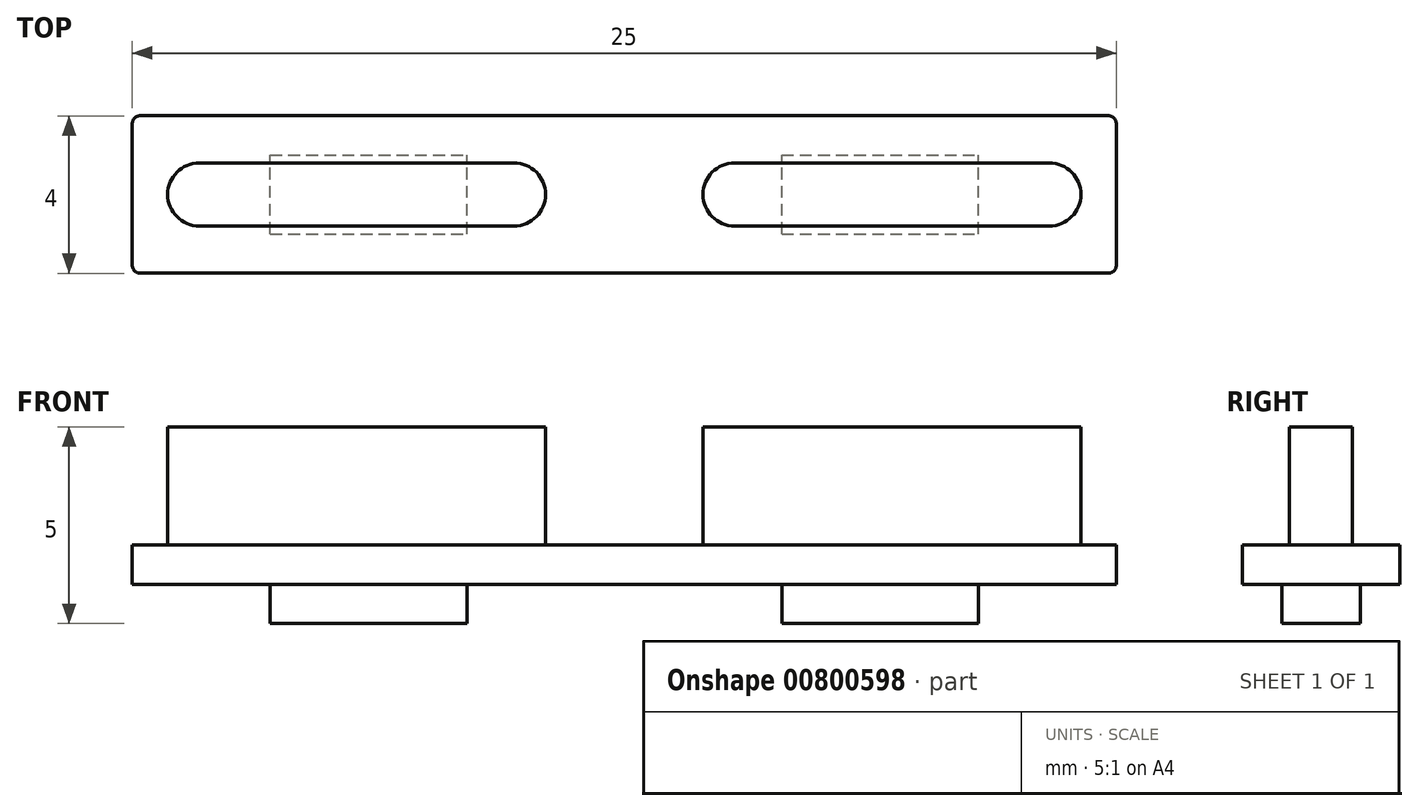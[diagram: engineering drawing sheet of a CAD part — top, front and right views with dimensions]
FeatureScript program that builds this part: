
annotation { "Feature Type Name" : "Feature", "Feature Type Description" : "" }
export const myFeature = defineFeature(function(context is Context, id is Id, definition is map)
    precondition{}
    {
        {
            var Q0;
            Q0=qCreatedBy(makeId("Top.planeOp"),FACE);
            var sketch = newSketch(context, id + "F0", { "sketchPlane" : qUnion([Q0])});
            skLineSegment(sketch, "E0.bottom", {"start": v(-2.37, 0.77) * mm, "end": v(22.63, 0.77) * mm});
            skLineSegment(sketch, "E0.top", {"start": v(-2.37, -3.23) * mm, "end": v(22.63, -3.23) * mm});
            skLineSegment(sketch, "E0.left", {"start": v(-2.37, 0.77) * mm, "end": v(-2.37, -3.23) * mm});
            skLineSegment(sketch, "E0.right", {"start": v(22.63, 0.77) * mm, "end": v(22.63, -3.23) * mm});
            skLineSegment(sketch, "E1", {"start": v(10.13, 0.77) * mm, "end": v(10.13, -3.23) * mm, "construction": true});
            skSolve(sketch);
        }
        {
            var Q0;
            Q0 = qSketchRegion(id + "F0", true);
            extrude(context, id + "F1", {"entities" : qUnion([Q0]), "depth" : 1 * mm, "offsetDistance" : 25 * mm});
        }
        {
            var Q0;
            Q0=makeQuery(id+"F1.opExtrude","CAP_FACE",FACE,{"disambiguationData":[OSD([sQuery(id+"F0.wireOp",EDGE,"E0.bottom"),sQuery(id+"F0.wireOp",EDGE,"E0.top"),sQuery(id+"F0.wireOp",EDGE,"E0.left"),sQuery(id+"F0.wireOp",EDGE,"E0.right")])],"isStart":false});
            var sketch = newSketch(context, id + "F2", { "sketchPlane" : qUnion([Q0])});
            skLineSegment(sketch, "E2.top", {"start": v(-0.67, -2.03) * mm, "end": v(7.33, -2.03) * mm});
            skArc(sketch, "E3", {"start": v(7.33, -2.03) * mm, "mid": v(8.13, -1.23) * mm, "end": v(7.33, -0.43) * mm});
            skPoint(sketch, "E4", {"position": v(22.63, -1.23) * mm});
            skPoint(sketch, "E5", {"position": v(-2.37, -1.23) * mm});
            skLineSegment(sketch, "E6", {"start": v(22.63, -1.23) * mm, "end": v(-2.37, -1.23) * mm, "construction": true});
            skLineSegment(sketch, "E7", {"start": v(7.33, -0.43) * mm, "end": v(-0.67, -0.43) * mm});
            skArc(sketch, "E8", {"start": v(-0.67, -0.43) * mm, "mid": v(-1.47, -1.23) * mm, "end": v(-0.67, -2.03) * mm});
            skPoint(sketch, "E9", {"position": v(10.13, -3.23) * mm});
            skPoint(sketch, "E10", {"position": v(10.13, 0.77) * mm});
            skLineSegment(sketch, "E11", {"start": v(10.13, -3.23) * mm, "end": v(10.13, 0.77) * mm, "construction": true});
            skLineSegment(sketch, "E12.top", {"start": v(12.93, -2.03) * mm, "end": v(20.93, -2.03) * mm});
            skArc(sketch, "E13", {"start": v(20.93, -2.03) * mm, "mid": v(21.73, -1.23) * mm, "end": v(20.93, -0.43) * mm});
            skLineSegment(sketch, "E14", {"start": v(20.93, -0.43) * mm, "end": v(12.93, -0.43) * mm});
            skArc(sketch, "E15", {"start": v(12.93, -0.43) * mm, "mid": v(12.13, -1.23) * mm, "end": v(12.93, -2.03) * mm});
            skSolve(sketch);
        }
        {
            var Q0;
            Q0=makeQuery(id+"F2.imprint","IMPRINT",FACE,{"disambiguationData":[TD([[makeQuery(id+"F2.imprint","IMPRINT",EDGE,{"derivedFrom":sQuery(id+"F2.wireOp",EDGE,"E2.top")}),1.0]])]});
            var Q1;
            Q1=makeQuery(id+"F2.imprint","IMPRINT",FACE,{"disambiguationData":[TD([[makeQuery(id+"F2.imprint","IMPRINT",EDGE,{"derivedFrom":sQuery(id+"F2.wireOp",EDGE,"E12.top")}),1.0]])]});
            extrude(context, id + "F3", {"entities" : qUnion([Q0, Q1]), "operationType" : NewBodyOperationType.ADD, "depth" : 3 * mm, "offsetDistance" : 25 * mm});
        }
        {
            var Q0;
            Q0=makeQuery(id+"F1.opExtrude","SWEPT_EDGE",EDGE,{"disambiguationData":[OSD([sQuery(id+"F0.wireOp",EDGE,"E0.bottom"),sQuery(id+"F0.wireOp",EDGE,"E0.right")])]});
            var Q1;
            Q1=makeQuery(id+"F1.opExtrude","SWEPT_EDGE",EDGE,{"disambiguationData":[OSD([sQuery(id+"F0.wireOp",EDGE,"E0.top"),sQuery(id+"F0.wireOp",EDGE,"E0.right")])]});
            var Q2;
            Q2=makeQuery(id+"F1.opExtrude","SWEPT_EDGE",EDGE,{"disambiguationData":[OSD([sQuery(id+"F0.wireOp",EDGE,"E0.top"),sQuery(id+"F0.wireOp",EDGE,"E0.left")])]});
            var Q3;
            Q3=makeQuery(id+"F1.opExtrude","SWEPT_EDGE",EDGE,{"disambiguationData":[OSD([sQuery(id+"F0.wireOp",EDGE,"E0.bottom"),sQuery(id+"F0.wireOp",EDGE,"E0.left")])]});
            fillet(context, id + "F4", {"entities" : qUnion([Q0, Q1, Q2, Q3]), "radius" : 0.2 * mm, "tangentPropagation" : true, "allowEdgeOverflow" : false});
        }
        {
            var Q0;
            Q0=makeQuery(id+"F1.opExtrude","CAP_FACE",FACE,{"disambiguationData":[OSD([sQuery(id+"F0.wireOp",EDGE,"E0.bottom"),sQuery(id+"F0.wireOp",EDGE,"E0.top"),sQuery(id+"F0.wireOp",EDGE,"E0.left"),sQuery(id+"F0.wireOp",EDGE,"E0.right")])],"isStart":true});
            var sketch = newSketch(context, id + "F5", { "sketchPlane" : qUnion([Q0])});
            skLineSegment(sketch, "E16.bottom", {"start": v(1.13, 2.23) * mm, "end": v(6.13, 2.23) * mm});
            skLineSegment(sketch, "E16.top", {"start": v(1.13, 0.23) * mm, "end": v(6.13, 0.23) * mm});
            skLineSegment(sketch, "E16.left", {"start": v(1.13, 2.23) * mm, "end": v(1.13, 0.23) * mm});
            skLineSegment(sketch, "E16.right", {"start": v(6.13, 2.23) * mm, "end": v(6.13, 0.23) * mm});
            skLineSegment(sketch, "E17.bottom", {"start": v(14.13, 2.23) * mm, "end": v(19.13, 2.23) * mm});
            skLineSegment(sketch, "E17.top", {"start": v(14.13, 0.23) * mm, "end": v(19.13, 0.23) * mm});
            skLineSegment(sketch, "E17.left", {"start": v(14.13, 2.23) * mm, "end": v(14.13, 0.23) * mm});
            skLineSegment(sketch, "E17.right", {"start": v(19.13, 2.23) * mm, "end": v(19.13, 0.23) * mm});
            skPoint(sketch, "E18", {"position": v(-2.37, 1.23) * mm});
            skPoint(sketch, "E19", {"position": v(22.63, 1.23) * mm});
            skLineSegment(sketch, "E20", {"start": v(-2.37, 1.23) * mm, "end": v(22.63, 1.23) * mm, "construction": true});
            skSolve(sketch);
        }
        {
            var Q0;
            Q0=makeQuery(id+"F5.imprint","IMPRINT",FACE,{"disambiguationData":[TD([[makeQuery(id+"F5.imprint","IMPRINT",EDGE,{"derivedFrom":sQuery(id+"F5.wireOp",EDGE,"E16.bottom")}),-1.0]])]});
            var Q1;
            Q1=makeQuery(id+"F5.imprint","IMPRINT",FACE,{"disambiguationData":[TD([[makeQuery(id+"F5.imprint","IMPRINT",EDGE,{"derivedFrom":sQuery(id+"F5.wireOp",EDGE,"E17.bottom")}),-1.0]])]});
            extrude(context, id + "F6", {"entities" : qUnion([Q0, Q1]), "operationType" : NewBodyOperationType.ADD, "depth" : 1 * mm, "offsetDistance" : 25 * mm});
        }
    });
